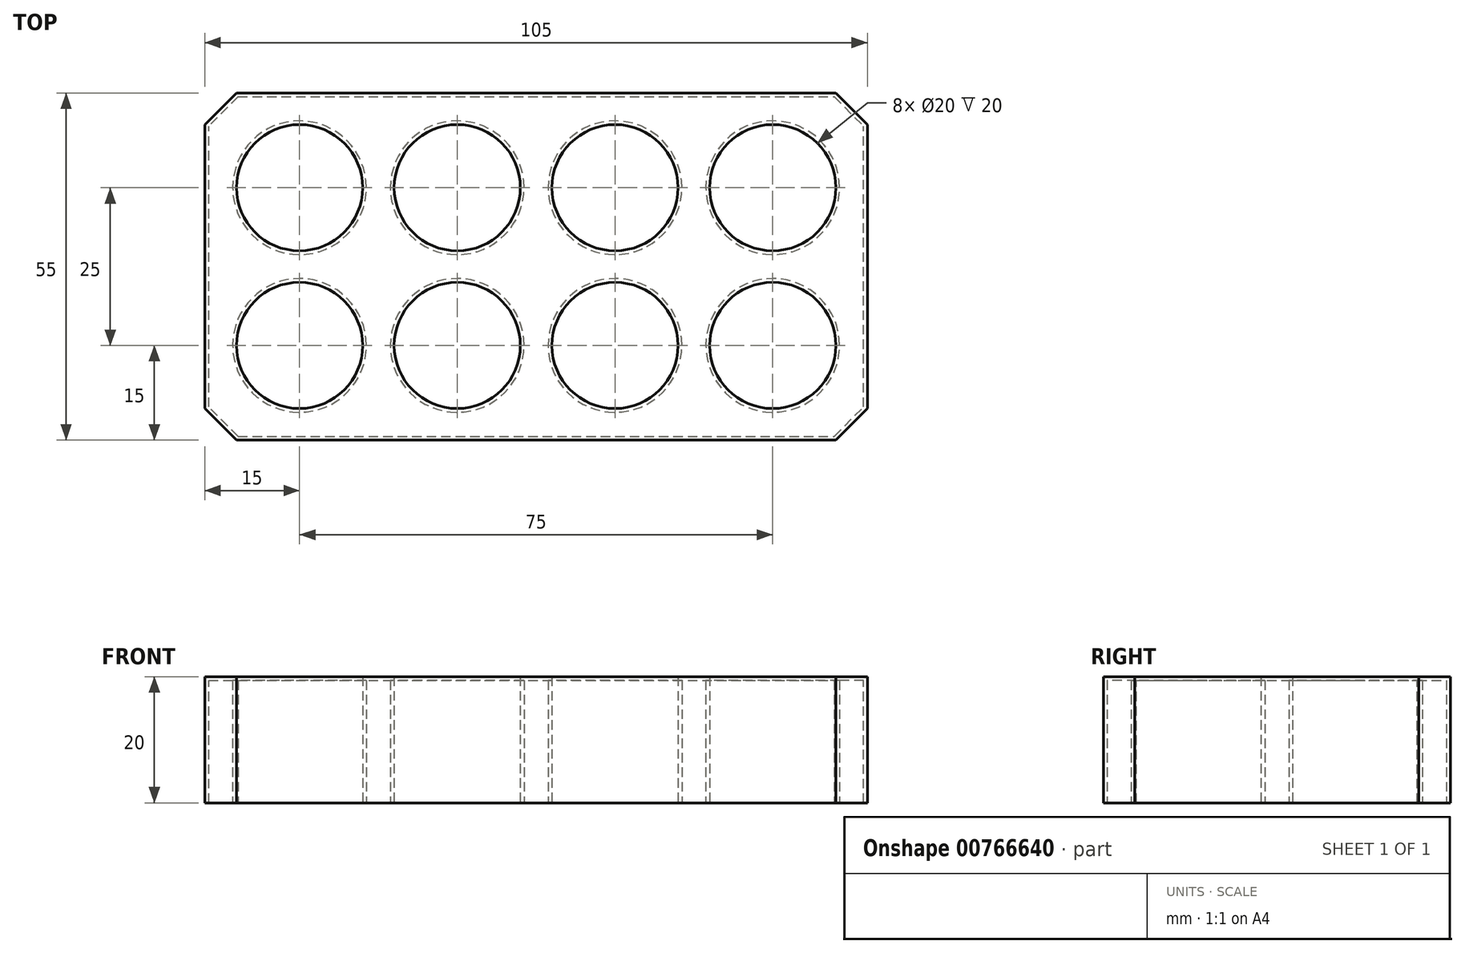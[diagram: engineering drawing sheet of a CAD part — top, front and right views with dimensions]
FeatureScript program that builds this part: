
annotation { "Feature Type Name" : "Feature", "Feature Type Description" : "" }
export const myFeature = defineFeature(function(context is Context, id is Id, definition is map)
    precondition{}
    {
        {
            var Q0;
            Q0=qCreatedBy(makeId("Top.planeOp"),FACE);
            var sketch = newSketch(context, id + "F0", { "sketchPlane" : qUnion([Q0])});
            skLineSegment(sketch, "E0.bottom", {"start": v(0, 0) * mm, "end": v(105, 0) * mm});
            skLineSegment(sketch, "E0.top", {"start": v(0, 55) * mm, "end": v(105, 55) * mm});
            skLineSegment(sketch, "E0.left", {"start": v(0, 0) * mm, "end": v(0, 55) * mm});
            skLineSegment(sketch, "E0.right", {"start": v(105, 0) * mm, "end": v(105, 55) * mm});
            skLineSegment(sketch, "E1", {"start": v(-47.06, 40) * mm, "end": v(194.02, 40) * mm, "construction": true});
            skLineSegment(sketch, "E2", {"start": v(-42.94, 15) * mm, "end": v(194.19, 15) * mm, "construction": true});
            skLineSegment(sketch, "E3", {"start": v(15, 40) * mm, "end": v(15, 15) * mm, "construction": true});
            skLineSegment(sketch, "E4", {"start": v(40, 40) * mm, "end": v(40, 15) * mm, "construction": true});
            skLineSegment(sketch, "E5", {"start": v(65, 40) * mm, "end": v(65, 15) * mm, "construction": true});
            skLineSegment(sketch, "E6", {"start": v(90, 40) * mm, "end": v(90, 15) * mm, "construction": true});
            skCircle(sketch, "E7", {"center": v(15, 40) * mm, "radius": 10 * mm});
            skCircle(sketch, "E8", {"center": v(40, 40) * mm, "radius": 10 * mm});
            skCircle(sketch, "E9", {"center": v(15, 15) * mm, "radius": 10 * mm});
            skCircle(sketch, "E10", {"center": v(40, 15) * mm, "radius": 10 * mm});
            skCircle(sketch, "E11", {"center": v(65, 15) * mm, "radius": 10 * mm});
            skCircle(sketch, "E12", {"center": v(65, 40) * mm, "radius": 10 * mm});
            skCircle(sketch, "E13", {"center": v(90, 40) * mm, "radius": 10 * mm});
            skCircle(sketch, "E14", {"center": v(90, 15) * mm, "radius": 10 * mm});
            skSolve(sketch);
        }
        {
            var Q0;
            Q0=makeQuery(id+"F0.imprint","IMPRINT",FACE,{"disambiguationData":[TD([[makeQuery(id+"F0.imprint","IMPRINT",EDGE,{"derivedFrom":sQuery(id+"F0.wireOp",EDGE,"E0.bottom")}),1.0]])]});
            extrude(context, id + "F1", {"entities" : qUnion([Q0]), "depth" : 20 * mm, "offsetDistance" : 25 * mm});
        }
        {
            var Q0;
            Q0=makeQuery(id+"F1.opExtrude","CAP_FACE",FACE,{"disambiguationData":[OSD([sQuery(id+"F0.wireOp",EDGE,"E0.bottom"),sQuery(id+"F0.wireOp",EDGE,"E0.top"),sQuery(id+"F0.wireOp",EDGE,"E0.left"),sQuery(id+"F0.wireOp",EDGE,"E0.right")])],"isStart":false});
            var sketch = newSketch(context, id + "F2", { "sketchPlane" : qUnion([Q0])});
            skCircle(sketch, "E15", {"center": v(20, 20) * mm, "radius": 10 * mm});
            skCircle(sketch, "E16", {"center": v(20, 55) * mm, "radius": 10 * mm});
            skCircle(sketch, "E17", {"center": v(55, 55) * mm, "radius": 10 * mm});
            skCircle(sketch, "E18", {"center": v(55, 20) * mm, "radius": 10 * mm});
            skLineSegment(sketch, "E19", {"start": v(20, 55) * mm, "end": v(293.88, 55) * mm, "construction": true});
            skPoint(sketch, "E20", {"position": v(156.94, 55) * mm});
            skLineSegment(sketch, "E21", {"start": v(20, 20) * mm, "end": v(20, 55) * mm, "construction": true});
            skLineSegment(sketch, "E22", {"start": v(55, 55) * mm, "end": v(55, 20) * mm, "construction": true});
            skLineSegment(sketch, "E23", {"start": v(20, 20) * mm, "end": v(226.78, 20) * mm, "construction": true});
            skLineSegment(sketch, "E24", {"start": v(90, 55) * mm, "end": v(90, 20) * mm, "construction": true});
            skLineSegment(sketch, "E25", {"start": v(125, 55) * mm, "end": v(125, 20) * mm, "construction": true});
            skCircle(sketch, "E26", {"center": v(90, 55) * mm, "radius": 10 * mm});
            skCircle(sketch, "E27", {"center": v(90, 20) * mm, "radius": 10 * mm});
            skCircle(sketch, "E28", {"center": v(125, 55) * mm, "radius": 10 * mm});
            skCircle(sketch, "E29", {"center": v(125, 20) * mm, "radius": 10 * mm});
            skSolve(sketch);
        }
        {
            var Q0;
            Q0=makeQuery(id+"F1.opExtrude","SWEPT_EDGE",EDGE,{"disambiguationData":[OSD([sQuery(id+"F0.wireOp",EDGE,"E0.bottom"),sQuery(id+"F0.wireOp",EDGE,"E0.left")])]});
            var Q1;
            Q1=makeQuery(id+"F1.opExtrude","SWEPT_EDGE",EDGE,{"disambiguationData":[OSD([sQuery(id+"F0.wireOp",EDGE,"E0.bottom"),sQuery(id+"F0.wireOp",EDGE,"E0.right")])]});
            var Q2;
            Q2=makeQuery(id+"F1.opExtrude","SWEPT_EDGE",EDGE,{"disambiguationData":[OSD([sQuery(id+"F0.wireOp",EDGE,"E0.top"),sQuery(id+"F0.wireOp",EDGE,"E0.right")])]});
            var Q3;
            Q3=makeQuery(id+"F1.opExtrude","SWEPT_EDGE",EDGE,{"disambiguationData":[OSD([sQuery(id+"F0.wireOp",EDGE,"E0.top"),sQuery(id+"F0.wireOp",EDGE,"E0.left")])]});
            chamfer(context, id + "F3", {"entities" : qUnion([Q0, Q1, Q2, Q3]), "width" : 5 * mm, "tangentPropagation" : true});
        }
        {
            var Q0;
            Q0=makeQuery(id+"F1.opExtrude","CAP_FACE",FACE,{"disambiguationData":[OSD([sQuery(id+"F0.wireOp",EDGE,"E0.bottom"),sQuery(id+"F0.wireOp",EDGE,"E0.top"),sQuery(id+"F0.wireOp",EDGE,"E0.left"),sQuery(id+"F0.wireOp",EDGE,"E0.right")])],"isStart":true});
            shell(context, id + "F4", {"entities" : qUnion([Q0]), "thickness" : .6 * mm});
        }
    });
